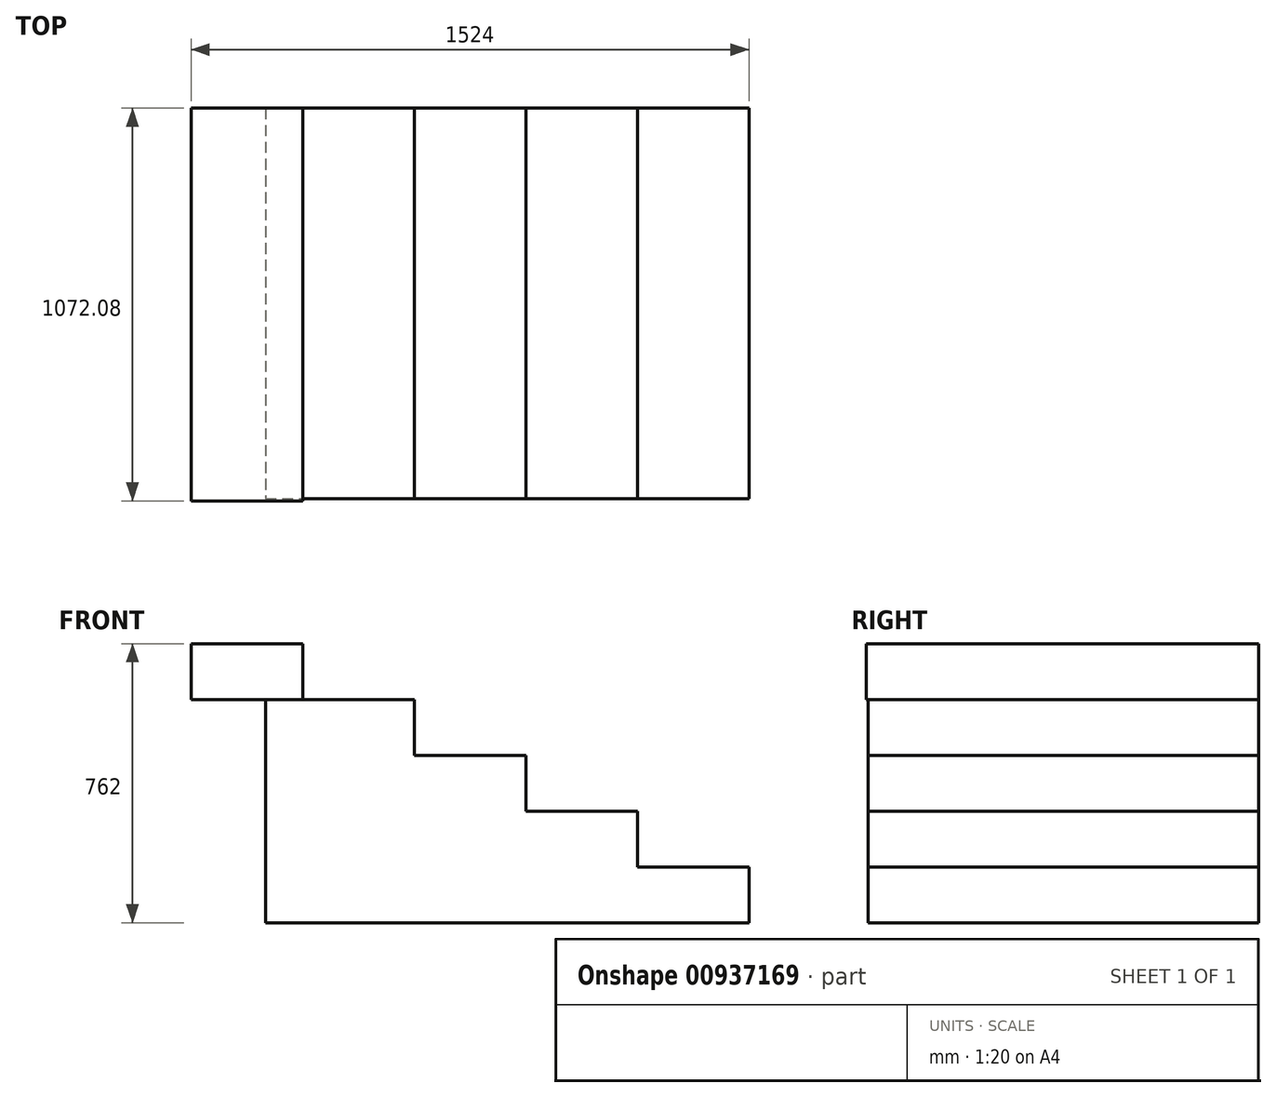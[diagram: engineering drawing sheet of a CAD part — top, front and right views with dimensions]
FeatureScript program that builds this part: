
annotation { "Feature Type Name" : "Feature", "Feature Type Description" : "" }
export const myFeature = defineFeature(function(context is Context, id is Id, definition is map)
    precondition{}
    {
        {
            var Q0;
            Q0=qCreatedBy(makeId("Top.planeOp"),FACE);
            var sketch = newSketch(context, id + "F0", { "sketchPlane" : qUnion([Q0])});
            skLineSegment(sketch, "E0.bottom", {"start": v(-653.53, 572.77) * mm, "end": v(667.27, 572.77) * mm});
            skLineSegment(sketch, "E0.top", {"start": v(-653.53, -494.03) * mm, "end": v(667.27, -494.03) * mm});
            skLineSegment(sketch, "E0.left", {"start": v(-653.53, 572.77) * mm, "end": v(-653.53, -494.03) * mm});
            skLineSegment(sketch, "E0.right", {"start": v(667.27, 572.77) * mm, "end": v(667.27, -494.03) * mm});
            skSolve(sketch);
        }
        {
            var Q0;
            Q0=makeQuery(id+"F0.imprint","IMPRINT",FACE,{"disambiguationData":[TD([[makeQuery(id+"F0.imprint","IMPRINT",EDGE,{"derivedFrom":sQuery(id+"F0.wireOp",EDGE,"E0.bottom")}),-1.0]])]});
            var Q1;
            Q1=sQuery(id+"F0.wireOp",EDGE,"E0.bottom");
            var Q2;
            Q2 = qBodyType(qCreatedBy(id + "F0" ,EDGE), BodyType.WIRE);
            extrude(context, id + "F1", {"entities" : qUnion([Q0]), "surfaceEntities" : qUnion([Q1, Q2]), "depth" : 152.4 * mm, "offsetDistance" : 25.4 * mm});
        }
        {
            var Q0;
            Q0=makeQuery(id+"F1.opExtrude","CAP_FACE",FACE,{"disambiguationData":[OSD([sQuery(id+"F0.wireOp",EDGE,"E0.bottom"),sQuery(id+"F0.wireOp",EDGE,"E0.top"),sQuery(id+"F0.wireOp",EDGE,"E0.left"),sQuery(id+"F0.wireOp",EDGE,"E0.right")])],"isStart":false});
            var sketch = newSketch(context, id + "F2", { "sketchPlane" : qUnion([Q0])});
            skLineSegment(sketch, "E1.bottom", {"start": v(-653.53, 572.77) * mm, "end": v(362.47, 572.77) * mm});
            skLineSegment(sketch, "E1.top", {"start": v(-653.53, -494.03) * mm, "end": v(362.47, -494.03) * mm});
            skLineSegment(sketch, "E1.left", {"start": v(-653.53, 572.77) * mm, "end": v(-653.53, -494.03) * mm});
            skLineSegment(sketch, "E1.right", {"start": v(362.47, 572.77) * mm, "end": v(362.47, -494.03) * mm});
            skSolve(sketch);
        }
        {
            var Q0;
            Q0 = qSketchRegion(id + "F2", true);
            extrude(context, id + "F3", {"entities" : qUnion([Q0]), "operationType" : NewBodyOperationType.ADD, "depth" : 152.4 * mm, "offsetDistance" : 25.4 * mm});
        }
        {
            var Q0;
            Q0=makeQuery(id+"F3.opExtrude","CAP_FACE",FACE,{"disambiguationData":[OSD([sQuery(id+"F2.wireOp",EDGE,"E1.bottom"),sQuery(id+"F2.wireOp",EDGE,"E1.top"),sQuery(id+"F2.wireOp",EDGE,"E1.left"),sQuery(id+"F2.wireOp",EDGE,"E1.right")])],"isStart":false});
            var sketch = newSketch(context, id + "F4", { "sketchPlane" : qUnion([Q0])});
            skLineSegment(sketch, "E2.bottom", {"start": v(-653.53, 572.77) * mm, "end": v(57.67, 572.77) * mm});
            skLineSegment(sketch, "E2.top", {"start": v(-653.53, -494.03) * mm, "end": v(57.67, -494.03) * mm});
            skLineSegment(sketch, "E2.left", {"start": v(-653.53, 572.77) * mm, "end": v(-653.53, -494.03) * mm});
            skLineSegment(sketch, "E2.right", {"start": v(57.67, 572.77) * mm, "end": v(57.67, -494.03) * mm});
            skSolve(sketch);
        }
        {
            var Q0;
            Q0 = qSketchRegion(id + "F4", true);
            extrude(context, id + "F5", {"entities" : qUnion([Q0]), "operationType" : NewBodyOperationType.ADD, "depth" : 152.4 * mm, "offsetDistance" : 25.4 * mm});
        }
        {
            var Q0;
            Q0=makeQuery(id+"F5.opExtrude","CAP_FACE",FACE,{"disambiguationData":[OSD([sQuery(id+"F4.wireOp",EDGE,"E2.bottom"),sQuery(id+"F4.wireOp",EDGE,"E2.top"),sQuery(id+"F4.wireOp",EDGE,"E2.left"),sQuery(id+"F4.wireOp",EDGE,"E2.right")])],"isStart":false});
            var sketch = newSketch(context, id + "F6", { "sketchPlane" : qUnion([Q0])});
            skLineSegment(sketch, "E3.bottom", {"start": v(-653.53, 572.77) * mm, "end": v(-247.13, 572.77) * mm});
            skLineSegment(sketch, "E3.top", {"start": v(-653.53, -494.03) * mm, "end": v(-247.13, -494.03) * mm});
            skLineSegment(sketch, "E3.left", {"start": v(-653.53, 572.77) * mm, "end": v(-653.53, -494.03) * mm});
            skLineSegment(sketch, "E3.right", {"start": v(-247.13, 572.77) * mm, "end": v(-247.13, -494.03) * mm});
            skSolve(sketch);
        }
        {
            var Q0;
            Q0 = qSketchRegion(id + "F6", true);
            extrude(context, id + "F7", {"entities" : qUnion([Q0]), "operationType" : NewBodyOperationType.ADD, "depth" : 152.4 * mm, "offsetDistance" : 25.4 * mm});
        }
        {
            var Q0;
            Q0=makeQuery(id+"F7.opExtrude","CAP_FACE",FACE,{"disambiguationData":[OSD([sQuery(id+"F6.wireOp",EDGE,"E3.bottom"),sQuery(id+"F6.wireOp",EDGE,"E3.top"),sQuery(id+"F6.wireOp",EDGE,"E3.left"),sQuery(id+"F6.wireOp",EDGE,"E3.right")])],"isStart":false});
            var sketch = newSketch(context, id + "F8", { "sketchPlane" : qUnion([Q0])});
            skLineSegment(sketch, "E4", {"start": v(-551.93, 572.77) * mm, "end": v(-653.53, 572.77) * mm});
            skLineSegment(sketch, "E5.bottom", {"start": v(-551.93, 572.77) * mm, "end": v(-856.73, 572.77) * mm});
            skLineSegment(sketch, "E5.top", {"start": v(-551.93, -499.31) * mm, "end": v(-856.73, -499.31) * mm});
            skLineSegment(sketch, "E5.left", {"start": v(-551.93, 572.77) * mm, "end": v(-551.93, -499.31) * mm});
            skLineSegment(sketch, "E5.right", {"start": v(-856.73, 572.77) * mm, "end": v(-856.73, -499.31) * mm});
            skSolve(sketch);
        }
        {
            var Q0;
            Q0 = qSketchRegion(id + "F8", true);
            extrude(context, id + "F9", {"entities" : qUnion([Q0]), "operationType" : NewBodyOperationType.ADD, "depth" : 152.4 * mm, "offsetDistance" : 25.4 * mm});
        }
    });
